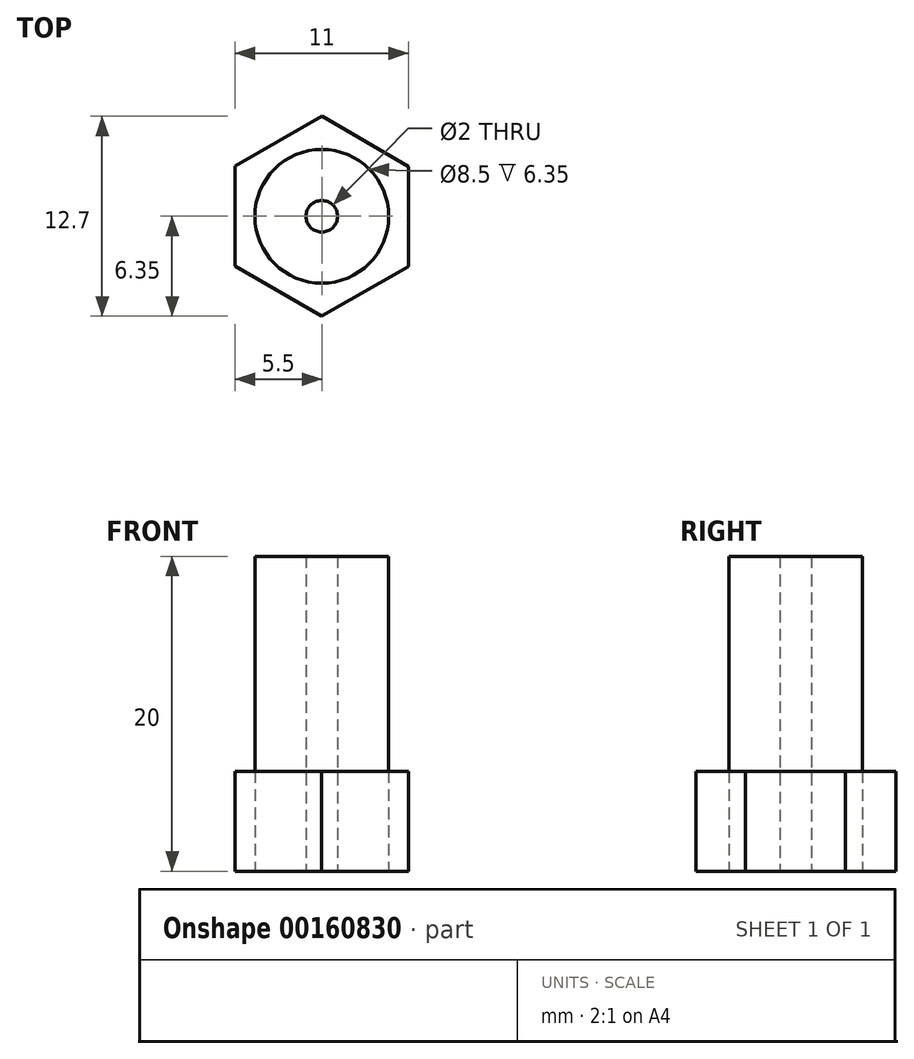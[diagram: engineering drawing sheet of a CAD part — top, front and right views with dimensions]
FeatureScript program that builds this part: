
annotation { "Feature Type Name" : "Feature", "Feature Type Description" : "" }
export const myFeature = defineFeature(function(context is Context, id is Id, definition is map)
    precondition{}
    {
        {
            var Q0;
            Q0=qCreatedBy(makeId("Top.planeOp"),FACE);
            var sketch = newSketch(context, id + "F0", { "sketchPlane" : qUnion([Q0])});
            skLineSegment(sketch, "E0.0", {"start": v(0, 6.35) * mm, "end": v(5.5, 3.17) * mm});
            skLineSegment(sketch, "E0.1", {"start": v(5.5, 3.17) * mm, "end": v(5.5, -3.18) * mm});
            skLineSegment(sketch, "E0.2", {"start": v(5.5, -3.18) * mm, "end": v(0, -6.35) * mm});
            skLineSegment(sketch, "E0.3", {"start": v(0, -6.35) * mm, "end": v(-5.5, -3.17) * mm});
            skLineSegment(sketch, "E0.4", {"start": v(-5.5, -3.17) * mm, "end": v(-5.5, 3.18) * mm});
            skLineSegment(sketch, "E0.5", {"start": v(-5.5, 3.18) * mm, "end": v(0, 6.35) * mm});
            skPoint(sketch, "E0.0.midPoint", {"position": v(2.75, 4.76) * mm});
            skCircle(sketch, "E1", {"center": v(0, 0) * mm, "radius": 4.25 * mm});
            skCircle(sketch, "E2", {"center": v(0, 0) * mm, "radius": 1 * mm});
            skSolve(sketch);
        }
        {
            var Q0;
            Q0=makeQuery(id+"F0.imprint","IMPRINT",FACE,{"disambiguationData":[TD([[makeQuery(id+"F0.imprint","IMPRINT",EDGE,{"derivedFrom":sQuery(id+"F0.wireOp",EDGE,"a37b7317-9f51-4ab7-9319-cc5c32cbad5e.0")}),-1.0]])]});
            var Q1;
            Q1=makeQuery(id+"F0.imprint","IMPRINT",FACE,{"disambiguationData":[TD([[makeQuery(id+"F0.imprint","IMPRINT",EDGE,{"derivedFrom":sQuery(id+"F0.wireOp",EDGE,"badf4bda-e46a-4685-932b-5e2a79928784.0")}),-1.0]])]});
            var Q2;
            Q2=makeQuery(id+"F0.imprint","IMPRINT",FACE,{"disambiguationData":[TD([[makeQuery(id+"F0.imprint","IMPRINT",EDGE,{"derivedFrom":sQuery(id+"F0.wireOp",EDGE,"2dd1fe61-1023-43b8-8558-c3a4b8e4237a.0")}),-1.0]])]});
            var Q3;
            Q3=makeQuery(id+"F0.imprint","IMPRINT",FACE,{"disambiguationData":[TD([[makeQuery(id+"F0.imprint","IMPRINT",EDGE,{"derivedFrom":sQuery(id+"F0.wireOp",EDGE,"E0.0")}),-1.0]])]});
            var Q4;
            Q4=makeQuery(id+"F0.imprint","IMPRINT",FACE,{"disambiguationData":[TD([[makeQuery(id+"F0.imprint","IMPRINT",EDGE,{"derivedFrom":sQuery(id+"F0.wireOp",EDGE,"fac3d89b-e944-48fd-9eba-d66cb260f058.0")}),-1.0]])]});
            var Q5;
            Q5=makeQuery(id+"F0.imprint","IMPRINT",FACE,{"disambiguationData":[TD([[makeQuery(id+"F0.imprint","IMPRINT",EDGE,{"derivedFrom":sQuery(id+"F0.wireOp",EDGE,"d38fd20a-7a6a-4ab5-95ec-18b69d0ceea4.0")}),-1.0]])]});
            extrude(context, id + "F1", {"entities" : qUnion([Q0, Q1, Q2, Q3, Q4, Q5]), "depth" : 6.35 * mm});
        }
        {
            var Q0;
            Q0=makeQuery(id+"F0.imprint","IMPRINT",FACE,{"disambiguationData":[TD([[makeQuery(id+"F0.imprint","IMPRINT",EDGE,{"derivedFrom":sQuery(id+"F0.wireOp",EDGE,"c54231f2-1cef-4e9a-ad0f-71994e32be5e")}),1.0]])]});
            var Q1;
            Q1=makeQuery(id+"F0.imprint","IMPRINT",FACE,{"disambiguationData":[TD([[makeQuery(id+"F0.imprint","IMPRINT",EDGE,{"derivedFrom":sQuery(id+"F0.wireOp",EDGE,"9007dbe4-c170-4375-9fba-45dfe89e6cb6")}),1.0]])]});
            var Q2;
            Q2=makeQuery(id+"F0.imprint","IMPRINT",FACE,{"disambiguationData":[TD([[makeQuery(id+"F0.imprint","IMPRINT",EDGE,{"derivedFrom":sQuery(id+"F0.wireOp",EDGE,"349da38b-2304-4277-bb7c-e390d0e36551")}),1.0]])]});
            var Q3;
            Q3=makeQuery(id+"F0.imprint","IMPRINT",FACE,{"disambiguationData":[TD([[makeQuery(id+"F0.imprint","IMPRINT",EDGE,{"derivedFrom":sQuery(id+"F0.wireOp",EDGE,"E1")}),1.0]])]});
            var Q4;
            Q4=makeQuery(id+"F0.imprint","IMPRINT",FACE,{"disambiguationData":[TD([[makeQuery(id+"F0.imprint","IMPRINT",EDGE,{"derivedFrom":sQuery(id+"F0.wireOp",EDGE,"ee792beb-a255-410c-808e-0c010578dbdd")}),1.0]])]});
            var Q5;
            Q5=makeQuery(id+"F0.imprint","IMPRINT",FACE,{"disambiguationData":[TD([[makeQuery(id+"F0.imprint","IMPRINT",EDGE,{"derivedFrom":sQuery(id+"F0.wireOp",EDGE,"51f9dfe1-3723-4feb-863f-59c88620304a")}),1.0]])]});
            extrude(context, id + "F2", {"entities" : qUnion([Q0, Q1, Q2, Q3, Q4, Q5]), "depth" : 20 * mm});
        }
    });
